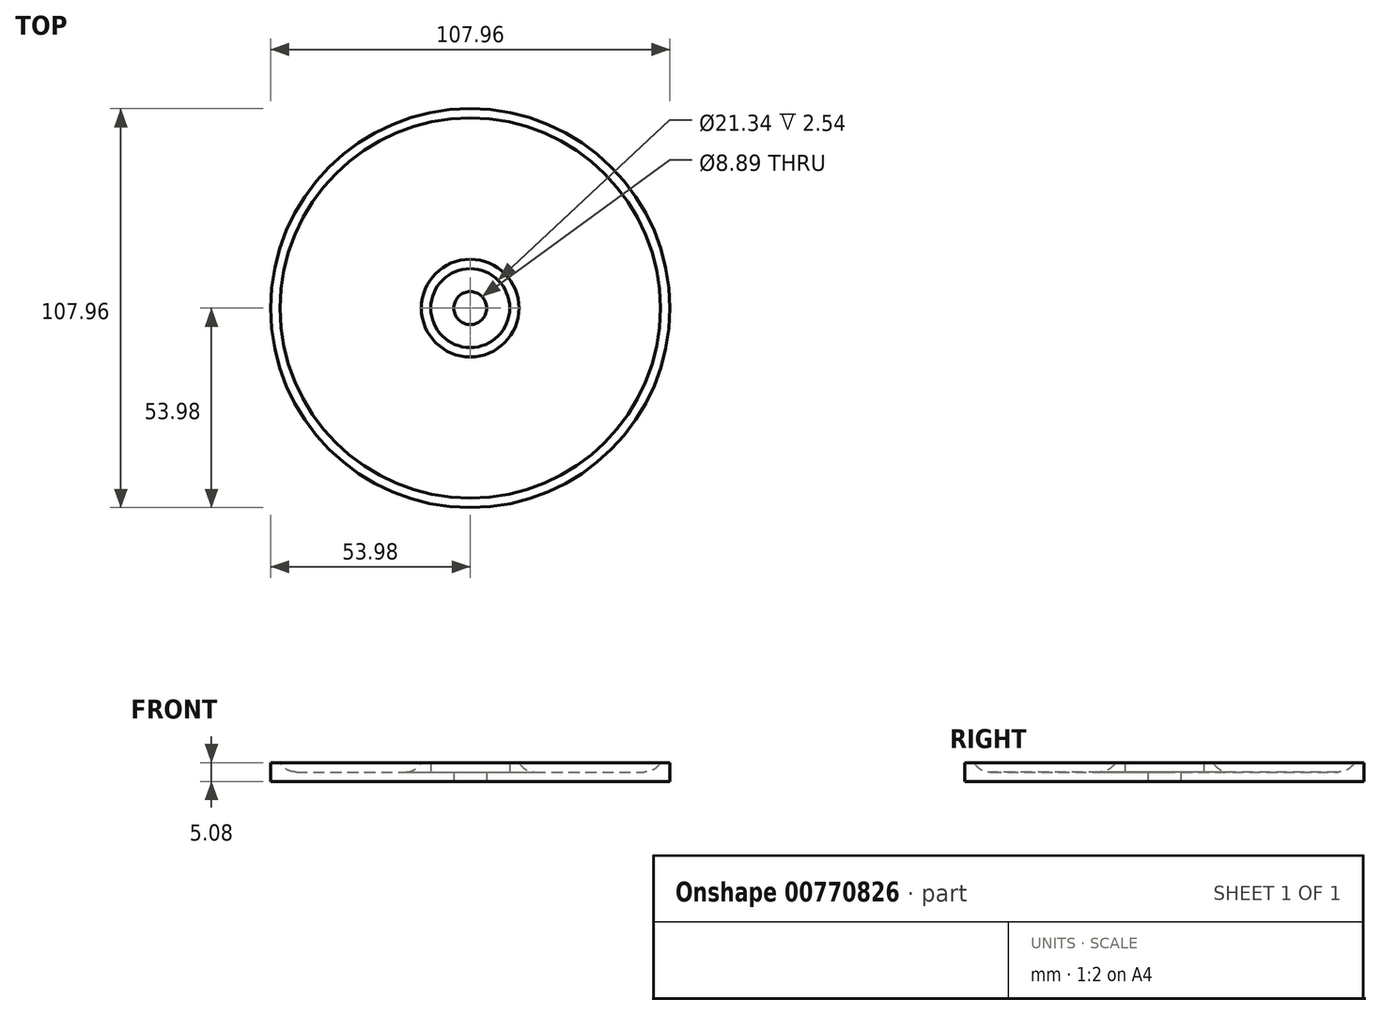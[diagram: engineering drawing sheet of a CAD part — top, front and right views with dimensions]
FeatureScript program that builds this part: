
annotation { "Feature Type Name" : "Feature", "Feature Type Description" : "" }
export const myFeature = defineFeature(function(context is Context, id is Id, definition is map)
    precondition{}
    {
        {
            var Q0;
            Q0=qCreatedBy(makeId("Right.planeOp"),FACE);
            var sketch = newSketch(context, id + "F0", { "sketchPlane" : qUnion([Q0])});
            skLineSegment(sketch, "E0.bottom", {"start": v(4.45, 0) * mm, "end": v(53.98, 0) * mm});
            skLineSegment(sketch, "E0.top", {"start": v(10.67, 5.08) * mm, "end": v(53.98, 5.08) * mm});
            skLineSegment(sketch, "E0.left", {"start": v(4.45, 0) * mm, "end": v(4.45, 2.54) * mm});
            skLineSegment(sketch, "E0.right", {"start": v(53.98, 0) * mm, "end": v(53.98, 5.08) * mm});
            skPoint(sketch, "E1.oppositeSnap0", {"position": v(4.45, 2.54) * mm});
            skLineSegment(sketch, "E1.top", {"start": v(4.45, 2.54) * mm, "end": v(10.67, 2.54) * mm});
            skLineSegment(sketch, "E1.right", {"start": v(10.67, 5.08) * mm, "end": v(10.67, 2.54) * mm});
            skLineSegment(sketch, "E2", {"start": v(0, 0) * mm, "end": v(0, 15.2) * mm, "construction": true});
            skSolve(sketch);
        }
        {
            var Q0;
            Q0=makeQuery(id+"F0.imprint","IMPRINT",FACE,{"disambiguationData":[TD([[makeQuery(id+"F0.imprint","IMPRINT",EDGE,{"derivedFrom":sQuery(id+"F0.wireOp",EDGE,"E0.bottom")}),1.0]])]});
            var Q1;
            Q1=sQuery(id+"F0.wireOp",EDGE,"E2");
            revolve(context, id + "F1", {"surfaceOperationType" : NewSurfaceOperationType.NEW, "entities" : qUnion([Q0]), "axis" : qUnion([Q1]), "revolveType" : RevolveType.FULL});
        }
        {
            var Q0;
            Q0=makeQuery(id+"F1.opRevolve","SWEPT_FACE",FACE,{"disambiguationData":[OSD([sQuery(id+"F0.wireOp",EDGE,"E0.top")])]});
            shell(context, id + "F2", {"entities" : qUnion([Q0]), "thickness" : 2.54 * mm});
        }
        {
            var Q0;
            Q0=makeQuery(id+"F2.opShell","OFFSET_EDGE",EDGE,{"disambiguationData":[OSD([sQuery(id+"F0.wireOp",EDGE,"E0.bottom"),sQuery(id+"F0.wireOp",EDGE,"E0.right")])]});
            var Q1;
            Q1=makeQuery(id+"F2.opShell","TWEAK_EDGE",EDGE,{"derivedFrom":[makeQuery(id+"F1.opRevolve","SWEPT_FACE",FACE,{"disambiguationData":[OSD([sQuery(id+"F0.wireOp",EDGE,"E0.bottom")])]}),makeQuery(id+"F1.opRevolve","SWEPT_FACE",FACE,{"disambiguationData":[OSD([sQuery(id+"F0.wireOp",EDGE,"E1.right")])]})]});
            fillet(context, id + "F3", {"entities" : qUnion([Q0, Q1]), "radius" : 5.08 * mm, "tangentPropagation" : true, "allowEdgeOverflow" : false});
        }
    });
